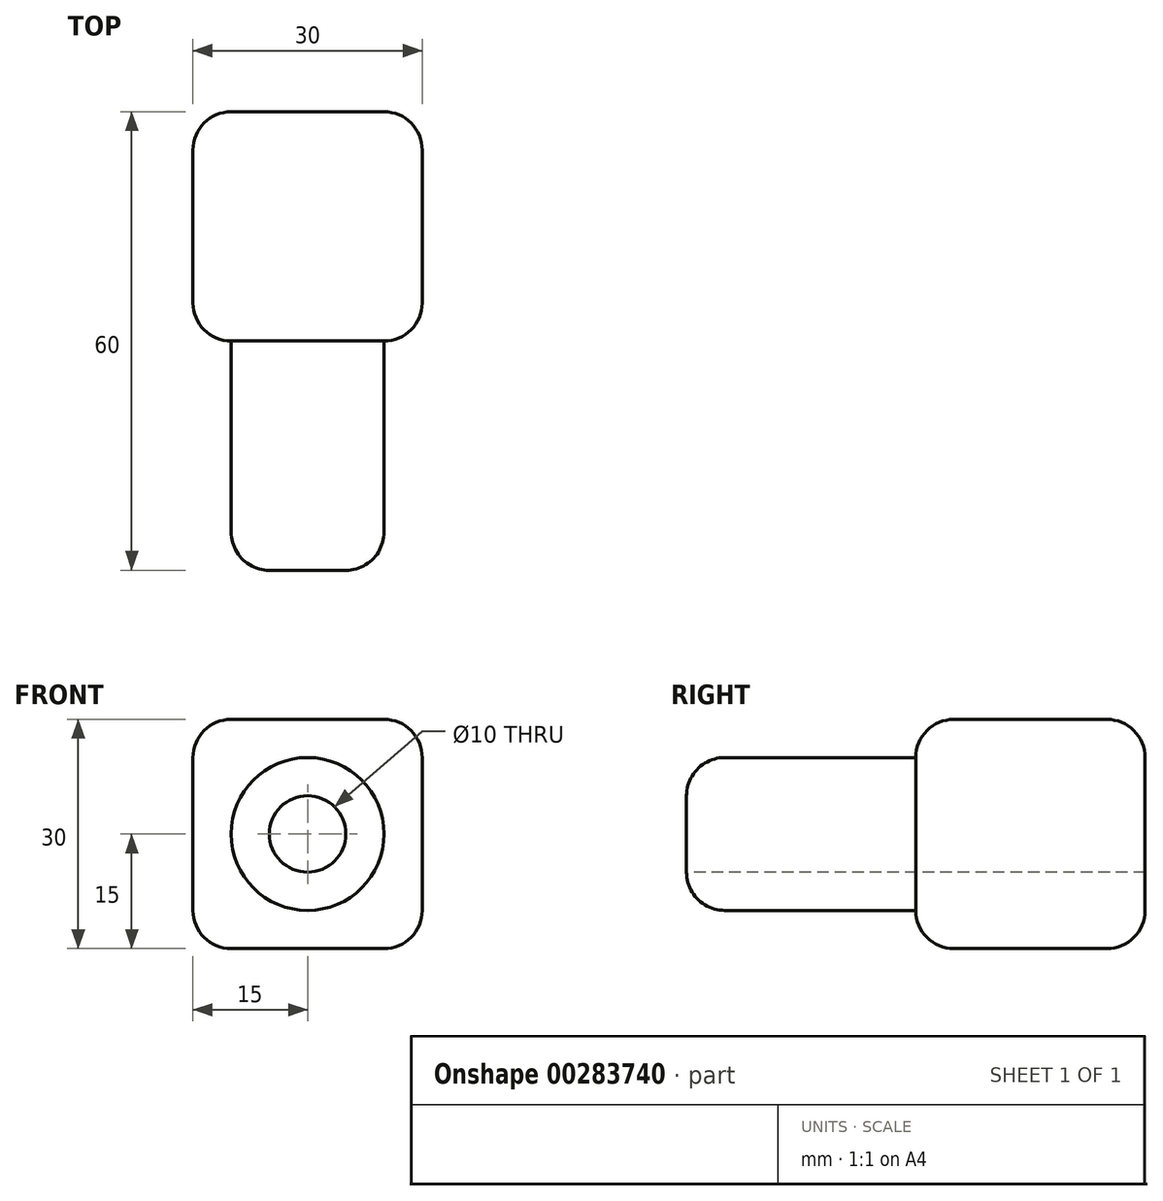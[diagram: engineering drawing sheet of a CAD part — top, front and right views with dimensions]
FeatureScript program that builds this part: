
annotation { "Feature Type Name" : "Feature", "Feature Type Description" : "" }
export const myFeature = defineFeature(function(context is Context, id is Id, definition is map)
    precondition{}
    {
        {
            var Q0;
            Q0=qCreatedBy(makeId("Front.planeOp"),FACE);
            var sketch = newSketch(context, id + "F0", { "sketchPlane" : qUnion([Q0])});
            skLineSegment(sketch, "E0.bottom", {"start": v(15, 15) * mm, "end": v(-15, 15) * mm});
            skLineSegment(sketch, "E0.top", {"start": v(15, -15) * mm, "end": v(-15, -15) * mm});
            skLineSegment(sketch, "E0.left", {"start": v(15, 15) * mm, "end": v(15, -15) * mm});
            skLineSegment(sketch, "E0.right", {"start": v(-15, 15) * mm, "end": v(-15, -15) * mm});
            skPoint(sketch, "E0.middle", {"position": v(0, 0) * mm});
            skSolve(sketch);
        }
        {
            var Q0;
            Q0 = qSketchRegion(id + "F0", true);
            extrude(context, id + "F1", {"entities" : qUnion([Q0]), "depth" : 30 * mm});
        }
        {
            var Q0;
            Q0=makeQuery(id+"F1.opExtrude","CAP_FACE",FACE,{"disambiguationData":[OSD([sQuery(id+"F0.wireOp",EDGE,"E0.bottom"),sQuery(id+"F0.wireOp",EDGE,"E0.top"),sQuery(id+"F0.wireOp",EDGE,"E0.left"),sQuery(id+"F0.wireOp",EDGE,"E0.right")])],"isStart":false});
            var sketch = newSketch(context, id + "F2", { "sketchPlane" : qUnion([Q0])});
            skCircle(sketch, "E1", {"center": v(0, 0) * mm, "radius": 10 * mm});
            skSolve(sketch);
        }
        {
            var Q0;
            Q0 = qSketchRegion(id + "F2", true);
            extrude(context, id + "F3", {"entities" : qUnion([Q0]), "operationType" : NewBodyOperationType.ADD, "depth" : 30 * mm});
        }
        {
            var Q0;
            Q0=makeQuery(id+"F3.opExtrude","CAP_FACE",FACE,{"disambiguationData":[OSD([sQuery(id+"F2.wireOp",EDGE,"E1")])],"isStart":false});
            var sketch = newSketch(context, id + "F4", { "sketchPlane" : qUnion([Q0])});
            skCircle(sketch, "E2", {"center": v(0, 0) * mm, "radius": 5 * mm});
            skSolve(sketch);
        }
        {
            var Q0;
            Q0 = qSketchRegion(id + "F4", true);
            extrude(context, id + "F5", {"entities" : qUnion([Q0]), "operationType" : NewBodyOperationType.REMOVE, "endBound" : BoundingType.THROUGH_ALL, "oppositeDirection" : true, "depth" : 25 * mm});
        }
        {
            var Q0;
            Q0=makeQuery(id+"F1.opExtrude","CAP_EDGE",EDGE,{"disambiguationData":[OSD([sQuery(id+"F0.wireOp",EDGE,"E0.bottom")])],"isStart":false});
            var Q1;
            Q1=makeQuery(id+"F1.opExtrude","CAP_EDGE",EDGE,{"disambiguationData":[OSD([sQuery(id+"F0.wireOp",EDGE,"E0.right")])],"isStart":false});
            var Q2;
            Q2=makeQuery(id+"F1.opExtrude","CAP_EDGE",EDGE,{"disambiguationData":[OSD([sQuery(id+"F0.wireOp",EDGE,"E0.top")])],"isStart":false});
            var Q3;
            Q3=makeQuery(id+"F1.opExtrude","CAP_EDGE",EDGE,{"disambiguationData":[OSD([sQuery(id+"F0.wireOp",EDGE,"E0.left")])],"isStart":false});
            var Q4;
            Q4=makeQuery(id+"F1.opExtrude","SWEPT_EDGE",EDGE,{"disambiguationData":[OSD([sQuery(id+"F0.wireOp",EDGE,"E0.bottom"),sQuery(id+"F0.wireOp",EDGE,"E0.left")])]});
            var Q5;
            Q5=makeQuery(id+"F1.opExtrude","SWEPT_EDGE",EDGE,{"disambiguationData":[OSD([sQuery(id+"F0.wireOp",EDGE,"E0.top"),sQuery(id+"F0.wireOp",EDGE,"E0.left")])]});
            var Q6;
            Q6=makeQuery(id+"F1.opExtrude","CAP_EDGE",EDGE,{"disambiguationData":[OSD([sQuery(id+"F0.wireOp",EDGE,"E0.top")])],"isStart":true});
            var Q7;
            Q7=makeQuery(id+"F1.opExtrude","CAP_EDGE",EDGE,{"disambiguationData":[OSD([sQuery(id+"F0.wireOp",EDGE,"E0.right")])],"isStart":true});
            var Q8;
            Q8=makeQuery(id+"F1.opExtrude","CAP_EDGE",EDGE,{"disambiguationData":[OSD([sQuery(id+"F0.wireOp",EDGE,"E0.left")])],"isStart":true});
            var Q9;
            Q9=makeQuery(id+"F1.opExtrude","CAP_EDGE",EDGE,{"disambiguationData":[OSD([sQuery(id+"F0.wireOp",EDGE,"E0.bottom")])],"isStart":true});
            var Q10;
            Q10=makeQuery(id+"F1.opExtrude","SWEPT_EDGE",EDGE,{"disambiguationData":[OSD([sQuery(id+"F0.wireOp",EDGE,"E0.bottom"),sQuery(id+"F0.wireOp",EDGE,"E0.right")])]});
            var Q11;
            Q11=makeQuery(id+"F3.opExtrude","CAP_EDGE",EDGE,{"disambiguationData":[OSD([sQuery(id+"F2.wireOp",EDGE,"E1")])],"isStart":false});
            var Q12;
            Q12=makeQuery(id+"F1.opExtrude","SWEPT_EDGE",EDGE,{"disambiguationData":[OSD([sQuery(id+"F0.wireOp",EDGE,"E0.top"),sQuery(id+"F0.wireOp",EDGE,"E0.right")])]});
            fillet(context, id + "F6", {"entities" : qUnion([Q0, Q1, Q2, Q3, Q4, Q5, Q6, Q7, Q8, Q9, Q10, Q11, Q12]), "radius" : 5 * mm, "tangentPropagation" : true, "allowEdgeOverflow" : false});
        }
    });
